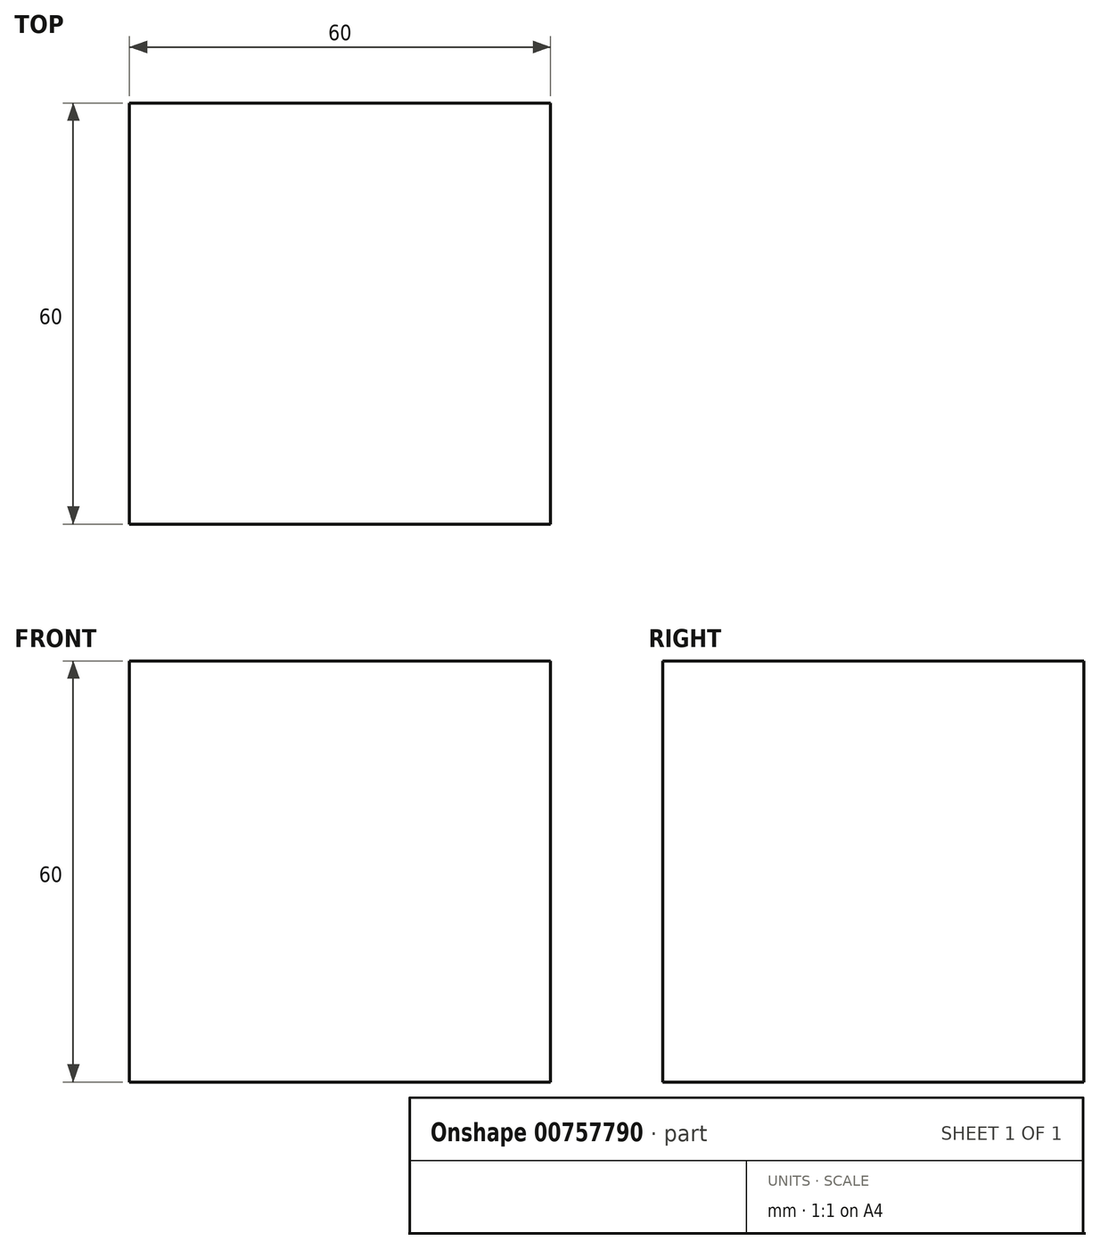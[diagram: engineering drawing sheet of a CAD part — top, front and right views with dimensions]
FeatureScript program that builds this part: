
annotation { "Feature Type Name" : "Feature", "Feature Type Description" : "" }
export const myFeature = defineFeature(function(context is Context, id is Id, definition is map)
    precondition{}
    {
        {
            var Q0;
            Q0=qCreatedBy(makeId("Front.planeOp"),FACE);
            var sketch = newSketch(context, id + "F0", { "sketchPlane" : qUnion([Q0])});
            skLineSegment(sketch, "E0.bottom", {"start": v(0, 0) * mm, "end": v(60, 0) * mm});
            skLineSegment(sketch, "E0.top", {"start": v(0, 60) * mm, "end": v(60, 60) * mm});
            skLineSegment(sketch, "E0.left", {"start": v(0, 0) * mm, "end": v(0, 60) * mm});
            skLineSegment(sketch, "E0.right", {"start": v(60, 0) * mm, "end": v(60, 60) * mm});
            skSolve(sketch);
        }
        {
            var Q0;
            Q0=makeQuery(id+"F0.imprint","IMPRINT",FACE,{"disambiguationData":[TD([[makeQuery(id+"F0.imprint","IMPRINT",EDGE,{"derivedFrom":sQuery(id+"F0.wireOp",EDGE,"E0.bottom")}),1.0]])]});
            extrude(context, id + "F1", {"entities" : qUnion([Q0]), "depth" : 60 * mm, "offsetDistance" : 25 * mm});
        }
    });
